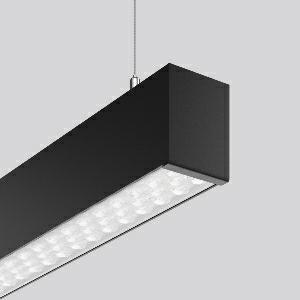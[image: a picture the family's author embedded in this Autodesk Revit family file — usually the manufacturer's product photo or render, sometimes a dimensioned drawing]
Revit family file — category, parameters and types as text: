
# Revit family: linedo_single_ip20_312564_003_1_5ea8
name_source: partatom
category: Lighting Fixtures
units: mm (PartAtom-declared; Revit-internal decimal feet)

## family parameters
Cut with Voids When Loaded = No
Host = Face
Light Source = No
Part Type = Normal
Room Calculation Point = No
Round Connector Dimension = Use Diameter
Shared = No

## types (1)
- LINEDO single IP20 (1 x LED Modul 840, 6450 lm, 4000)
    Apparent Load = 40 VA
    CIE Flux Codes = 86 96 99 100 100
    Color Rendering = 80
    Color Temperature = 4000
    Default Elevation = 1800 mm
    Description = Series: LINEDO single IP20
Stylish pendant luminaire. Housing: extruded aluminium profile, powder-coated. End cap aluminium powder-coated, without visible screws. High-efficiency LED units with optimum light control thanks to clear plastic (PC) lens optics. 2-point steel cable suspension freely positionable and infinitely height-adjustable. With power cord (2.5 m). Please order canopy separately if required. Perfect for office areas (RUG < 19) and environments with computer screens in accordance with EN 12464-1. 
Colour: deep black, matt (RAL 9005)
Length: 2264 mm
Width: 58 mm
Height: 76 mm
Suspension length: 100-1500 mm
Lamp: LED
Socket: without socket
Colour temperature: 4000K
Colour rendering index (CRI): 80
System power: 40 W
Rated luminous flux: 6450 lm
Beam angle Down: 59°
Luminous efficiency: 161 lm/W
Control gear: Regulated power supply
Protection class: I
Type of protection: IP 20
    Height = 76 mm
    Lamp = 1 x LED Modul 840
    Lamp Light Flux = 6450 lm
    Lamp count = 1
    Length = 2264 mm
    Lifetime = 50000 h
    Luminous efficacy = 161 lm/W
    Manufacturer = RZB
    ModVariant = No
    Model = 312564.003.1
    Mounting Place = Ceiling
    Mounting Type = Surface mounted, Pendant
    Number of Poles = 1
    OnlyDefault = Yes
    Power Factor = 1
    Product Name = LINEDO single IP20
    Product group = Pendant luminaires
    ProductGroupID = 902
    Protection Class = Protection class I
    Protection Degree = IP 20
    RLX_Detail_Level = 1
    RLX_Emergency_Light_Flux = 0 lm
    RLX_Emergency_Type = 0
    RLX_Emergency_Type_DB = No
    RlxData = <blob elided: 35005 chars, md5=2c19052b>
    Socket = socket
    Standby Power = 0 W
    System Light Flux = 6450 lm
    System Power = 40 W
    Type Comments = ALEA SPOT
    Type Image = 312563.003.jpg
    URL = http://relux.com
    VarID = ---
    Voltage = 230 V
    Voltage Range = 220-240 V
    Weight = 0.00 kg
    Width = 58 mm

## geometry (parser evidence)
native form markers: Blend x4, Sweep x10
no freeform markers — native parametric forms only
